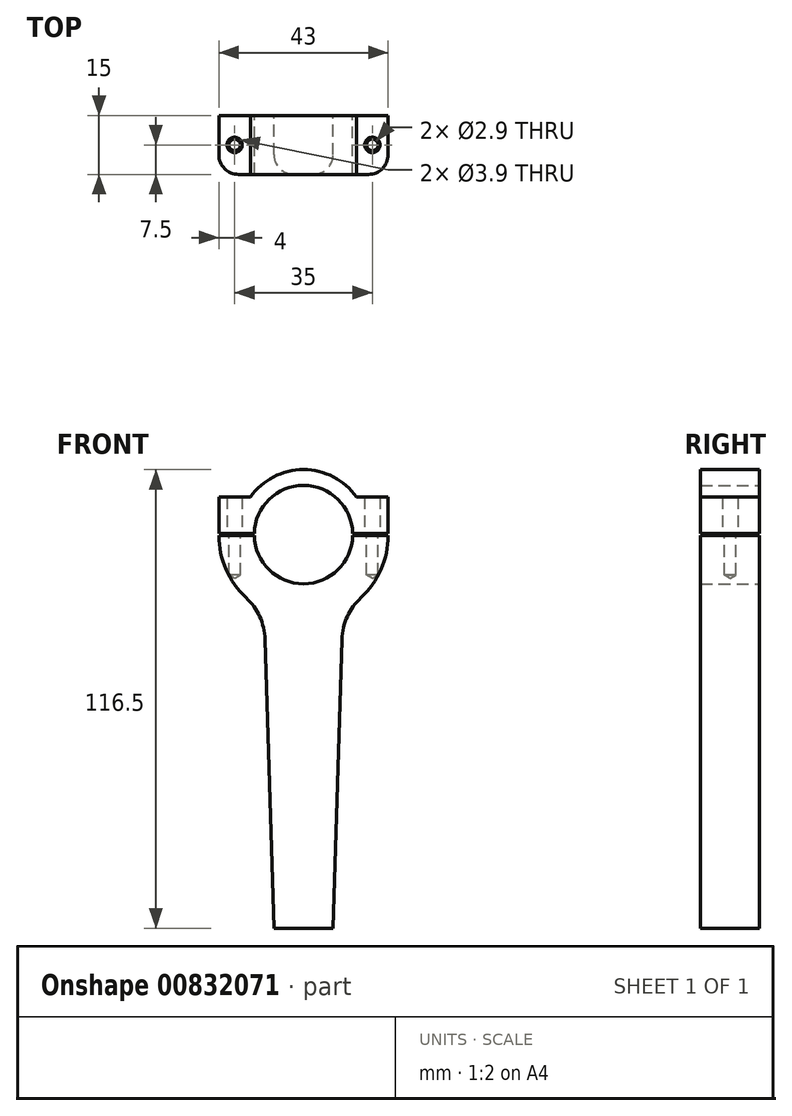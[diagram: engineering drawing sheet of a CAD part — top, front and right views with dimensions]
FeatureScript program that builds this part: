
annotation { "Feature Type Name" : "Feature", "Feature Type Description" : "" }
export const myFeature = defineFeature(function(context is Context, id is Id, definition is map)
    precondition{}
    {
        {
            var Q0;
            Q0=qCreatedBy(makeId("Front.planeOp"),FACE);
            var sketch = newSketch(context, id + "F0", { "sketchPlane" : qUnion([Q0])});
            skCircle(sketch, "E0", {"center": v(0, 0) * mm, "radius": 12.5 * mm, "construction": true});
            skLineSegment(sketch, "E1", {"start": v(-12.5, -0.25) * mm, "end": v(-21.5, -0.25) * mm});
            skLineSegment(sketch, "E2", {"start": v(-7.5, -100) * mm, "end": v(7.5, -100) * mm});
            skLineSegment(sketch, "E3", {"start": v(21.5, -0.25) * mm, "end": v(12.5, -0.25) * mm});
            skArc(sketch, "E4", {"start": v(-12.5, -0.25) * mm, "mid": v(0, -12.5) * mm, "end": v(12.5, -0.25) * mm});
            skLineSegment(sketch, "E5", {"start": v(-7.5, -100) * mm, "end": v(-10, -19.28) * mm});
            skLineSegment(sketch, "E6", {"start": v(7.5, -100) * mm, "end": v(10, -19.28) * mm});
            skArc(sketch, "E7", {"start": v(10, -19.28) * mm, "mid": v(18.4, -11.37) * mm, "end": v(21.5, -0.25) * mm});
            skArc(sketch, "E8", {"start": v(-21.5, -0.25) * mm, "mid": v(-18.4, -11.37) * mm, "end": v(-10, -19.28) * mm});
            skPoint(sketch, "E9", {"position": v(0, -100) * mm});
            skSolve(sketch);
        }
        {
            var Q0;
            Q0 = qSketchRegion(id + "F0", true);
            extrude(context, id + "F1", {"entities" : qUnion([Q0]), "endBound" : BoundingType.SYMMETRIC, "depth" : 15 * mm, "offsetDistance" : 25 * mm});
        }
        {
            var Q0;
            Q0=makeQuery(id+"F1.opExtrude","SWEPT_FACE",FACE,{"disambiguationData":[OSD([sQuery(id+"F0.wireOp",EDGE,"E1")])]});
            var sketch = newSketch(context, id + "F2", { "sketchPlane" : qUnion([Q0])});
            skPoint(sketch, "E10", {"position": v(-17.5, 0) * mm});
            skPoint(sketch, "E11", {"position": v(17.5, 0) * mm});
            skSolve(sketch);
        }
        {
            var Q0;
            Q0=sQuery(id+"F2.wireOp",VERTEX,"E10");
            var Q1;
            Q1=sQuery(id+"F2.wireOp",VERTEX,"E11");
            var Q2;
            Q2=makeQuery(id+"F1.opExtrude","SWEPT_BODY",BODY,{"disambiguationData":[OSD([sQuery(id+"F0.wireOp",EDGE,"E1"),sQuery(id+"F0.wireOp",EDGE,"E2"),sQuery(id+"F0.wireOp",EDGE,"E3"),sQuery(id+"F0.wireOp",EDGE,"E4"),sQuery(id+"F0.wireOp",EDGE,"E5"),sQuery(id+"F0.wireOp",EDGE,"E6"),sQuery(id+"F0.wireOp",EDGE,"E7"),sQuery(id+"F0.wireOp",EDGE,"E8")])]});
            hole(context, id + "F3", {"style" : HoleStyle.SIMPLE, "endStyle" : HoleEndStyle.BLIND, "holeDiameter" : 2.9 * mm, "majorDiameter" : 5 * mm, "holeDepth" : 10 * mm, "isTappedThrough" : true, "tappedDepth" : 12 * mm, "tapClearance" : 3, "locations" : qUnion([Q0, Q1]), "scope" : qUnion([Q2])});
        }
        {
            var Q0;
            Q0=makeQuery(id+"F1.opExtrude","SWEPT_EDGE",EDGE,{"disambiguationData":[OSD([sQuery(id+"F0.wireOp",EDGE,"E5"),sQuery(id+"F0.wireOp",EDGE,"E8")])]});
            var Q1;
            Q1=makeQuery(id+"F1.opExtrude","SWEPT_EDGE",EDGE,{"disambiguationData":[OSD([sQuery(id+"F0.wireOp",EDGE,"E6"),sQuery(id+"F0.wireOp",EDGE,"E7")])]});
            fillet(context, id + "F4", {"entities" : qUnion([Q0, Q1]), "radius" : 15 * mm, "tangentPropagation" : true, "allowEdgeOverflow" : false});
        }
        {
            var Q0;
            Q0=makeQuery(id+"F1.opExtrude","CAP_EDGE",EDGE,{"disambiguationData":[OSD([sQuery(id+"F0.wireOp",EDGE,"E5")])],"isStart":false});
            var Q1;
            Q1=makeQuery(id+"F1.opExtrude","CAP_EDGE",EDGE,{"disambiguationData":[OSD([sQuery(id+"F0.wireOp",EDGE,"E6")])],"isStart":false});
            fillet(context, id + "F5", {"entities" : qUnion([Q0, Q1]), "radius" : 5 * mm, "tangentPropagation" : true, "allowEdgeOverflow" : false});
        }
        {
            var Q0;
            Q0=qCreatedBy(makeId("Front.planeOp"),FACE);
            var sketch = newSketch(context, id + "F6", { "sketchPlane" : qUnion([Q0])});
            skLineSegment(sketch, "E12", {"start": v(-12.5, 0.25) * mm, "end": v(-21.5, 0.25) * mm});
            skLineSegment(sketch, "E13", {"start": v(-21.5, 0.25) * mm, "end": v(-21.5, 9.5) * mm});
            skLineSegment(sketch, "E14", {"start": v(-21.5, 9.5) * mm, "end": v(-13.5, 9.5) * mm});
            skArc(sketch, "E15", {"start": v(13.5, 9.5) * mm, "mid": v(0, 16.5) * mm, "end": v(-13.5, 9.5) * mm});
            skLineSegment(sketch, "E16", {"start": v(13.5, 9.5) * mm, "end": v(21.5, 9.5) * mm});
            skLineSegment(sketch, "E17", {"start": v(21.5, 9.5) * mm, "end": v(21.5, 0.25) * mm});
            skLineSegment(sketch, "E18", {"start": v(21.5, 0.25) * mm, "end": v(12.5, 0.25) * mm});
            skArc(sketch, "E19", {"start": v(12.5, 0.25) * mm, "mid": v(0, 12.5) * mm, "end": v(-12.5, 0.25) * mm});
            skSolve(sketch);
        }
        {
            var Q0;
            Q0 = qSketchRegion(id + "F6", true);
            extrude(context, id + "F7", {"entities" : qUnion([Q0]), "endBound" : BoundingType.SYMMETRIC, "depth" : 15 * mm, "offsetDistance" : 25 * mm});
        }
        {
            var Q0;
            Q0=sQuery(id+"F2.wireOp",VERTEX,"E10");
            var Q1;
            Q1=sQuery(id+"F2.wireOp",VERTEX,"E11");
            var Q2;
            Q2=makeQuery(id+"F7.opExtrude","SWEPT_BODY",BODY,{"disambiguationData":[OSD([sQuery(id+"F6.wireOp",EDGE,"E12"),sQuery(id+"F6.wireOp",EDGE,"E13"),sQuery(id+"F6.wireOp",EDGE,"E14"),sQuery(id+"F6.wireOp",EDGE,"E15"),sQuery(id+"F6.wireOp",EDGE,"E16"),sQuery(id+"F6.wireOp",EDGE,"E17"),sQuery(id+"F6.wireOp",EDGE,"E18"),sQuery(id+"F6.wireOp",EDGE,"E19")])]});
            hole(context, id + "F8", {"style" : HoleStyle.SIMPLE, "endStyle" : HoleEndStyle.THROUGH, "oppositeDirection" : true, "holeDiameter" : 3.9 * mm, "majorDiameter" : 5 * mm, "isTappedThrough" : true, "tappedDepth" : 12 * mm, "tapClearance" : 3, "locations" : qUnion([Q0, Q1]), "scope" : qUnion([Q2])});
        }
        {
            var Q0;
            Q0=makeQuery(id+"F7.opExtrude","CAP_EDGE",EDGE,{"disambiguationData":[OSD([sQuery(id+"F6.wireOp",EDGE,"E13")])],"isStart":false});
            var Q1;
            Q1=makeQuery(id+"F7.opExtrude","CAP_EDGE",EDGE,{"disambiguationData":[OSD([sQuery(id+"F6.wireOp",EDGE,"E17")])],"isStart":false});
            fillet(context, id + "F9", {"entities" : qUnion([Q0, Q1]), "radius" : 5 * mm, "tangentPropagation" : true, "allowEdgeOverflow" : false});
        }
    });
